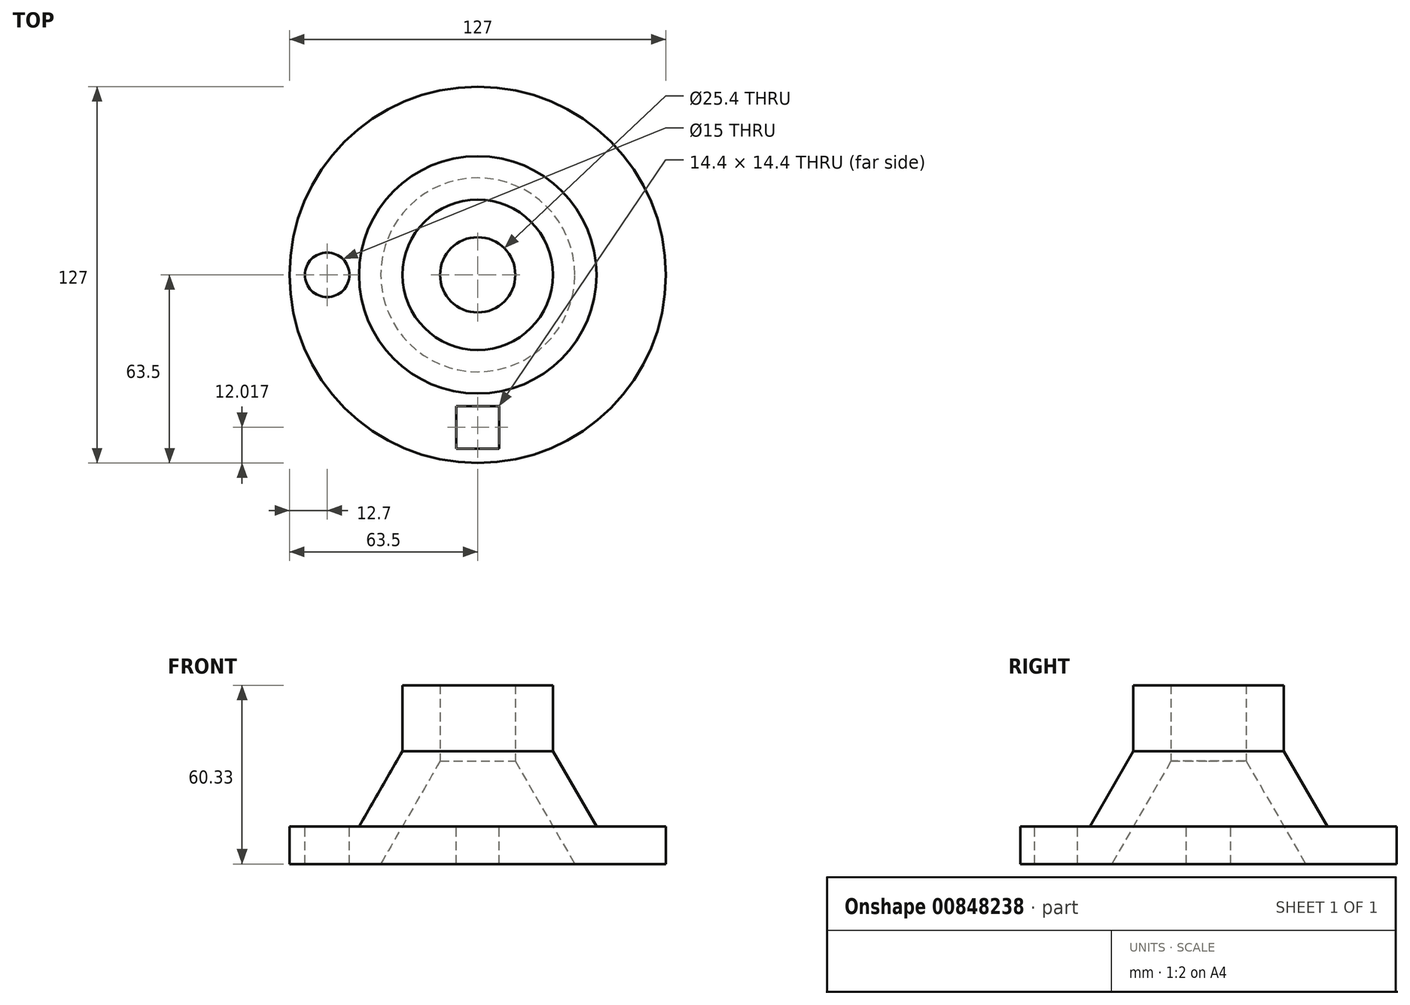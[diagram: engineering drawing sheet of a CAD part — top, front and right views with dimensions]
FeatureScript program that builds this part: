
annotation { "Feature Type Name" : "Feature", "Feature Type Description" : "" }
export const myFeature = defineFeature(function(context is Context, id is Id, definition is map)
    precondition{}
    {
        {
            var Q0;
            Q0=qCreatedBy(makeId("Front.planeOp"),FACE);
            var sketch = newSketch(context, id + "F0", { "sketchPlane" : qUnion([Q0])});
            skLineSegment(sketch, "E0", {"start": v(12.7, 60.32) * mm, "end": v(12.7, 34.7) * mm});
            skLineSegment(sketch, "E1", {"start": v(12.7, 34.7) * mm, "end": v(32.73, 0) * mm});
            skLineSegment(sketch, "E2", {"start": v(32.73, 0) * mm, "end": v(63.5, 0) * mm});
            skLineSegment(sketch, "E3", {"start": v(63.5, 0) * mm, "end": v(63.5, 12.7) * mm});
            skLineSegment(sketch, "E4", {"start": v(63.5, 12.7) * mm, "end": v(40.06, 12.7) * mm});
            skLineSegment(sketch, "E5", {"start": v(40.06, 12.7) * mm, "end": v(25.4, 38.1) * mm});
            skLineSegment(sketch, "E6", {"start": v(25.4, 38.1) * mm, "end": v(25.4, 60.32) * mm});
            skLineSegment(sketch, "E7", {"start": v(25.4, 60.32) * mm, "end": v(12.7, 60.32) * mm});
            skLineSegment(sketch, "E8", {"start": v(0, 0) * mm, "end": v(0, 37.93) * mm});
            skSolve(sketch);
        }
        {
            var Q0;
            Q0=makeQuery(id+"F0.imprint","IMPRINT",FACE,{"disambiguationData":[TD([[makeQuery(id+"F0.imprint","IMPRINT",EDGE,{"derivedFrom":sQuery(id+"F0.wireOp",EDGE,"E0")}),1.0]])]});
            var Q1;
            Q1=sQuery(id+"F0.wireOp",EDGE,"E8");
            revolve(context, id + "F1", {"surfaceOperationType" : NewSurfaceOperationType.NEW, "entities" : qUnion([Q0]), "axis" : qUnion([Q1]), "revolveType" : RevolveType.FULL});
        }
        {
            var Q0;
            Q0=makeQuery(id+"F1.opRevolve","SWEPT_FACE",FACE,{"disambiguationData":[OSD([sQuery(id+"F0.wireOp",EDGE,"E4")])]});
            var sketch = newSketch(context, id + "F2", { "sketchPlane" : qUnion([Q0])});
            skCircle(sketch, "E9", {"center": v(-50.8, 0) * mm, "radius": 7.5 * mm});
            skSolve(sketch);
        }
        {
            var Q0;
            Q0=makeQuery(id+"F2.imprint","IMPRINT",FACE,{"disambiguationData":[TD([[makeQuery(id+"F2.imprint","IMPRINT",EDGE,{"derivedFrom":sQuery(id+"F2.wireOp",EDGE,"E9")}),1.0]])]});
            extrude(context, id + "F3", {"entities" : qUnion([Q0]), "operationType" : NewBodyOperationType.REMOVE, "endBound" : BoundingType.THROUGH_ALL, "oppositeDirection" : true, "depth" : 25.4 * mm, "offsetDistance" : 25.4 * mm});
        }
        {
            var Q0;
            Q0=makeQuery(id+"F1.opRevolve","SWEPT_FACE",FACE,{"disambiguationData":[OSD([sQuery(id+"F0.wireOp",EDGE,"E4")])]});
            var sketch = newSketch(context, id + "F4", { "sketchPlane" : qUnion([Q0])});
            skCircle(sketch, "E10.cCircle", {"center": v(0, -51.48) * mm, "radius": 7.2 * mm, "construction": true});
            skLineSegment(sketch, "E10.0", {"start": v(7.2, -44.28) * mm, "end": v(7.2, -58.68) * mm});
            skLineSegment(sketch, "E10.1", {"start": v(7.2, -58.68) * mm, "end": v(-7.2, -58.68) * mm});
            skLineSegment(sketch, "E10.2", {"start": v(-7.2, -58.68) * mm, "end": v(-7.2, -44.28) * mm});
            skLineSegment(sketch, "E10.3", {"start": v(-7.2, -44.28) * mm, "end": v(7.2, -44.28) * mm});
            skPoint(sketch, "E10.0.midPoint", {"position": v(7.2, -51.48) * mm});
            skSolve(sketch);
        }
        {
            var Q0;
            Q0=makeQuery(id+"F4.imprint","IMPRINT",FACE,{"disambiguationData":[TD([[makeQuery(id+"F4.imprint","IMPRINT",EDGE,{"derivedFrom":sQuery(id+"F4.wireOp",EDGE,"E10.0")}),-1.0]])]});
            extrude(context, id + "F5", {"entities" : qUnion([Q0]), "operationType" : NewBodyOperationType.REMOVE, "endBound" : BoundingType.THROUGH_ALL, "oppositeDirection" : true, "depth" : 25.4 * mm, "offsetDistance" : 25.4 * mm});
        }
    });
